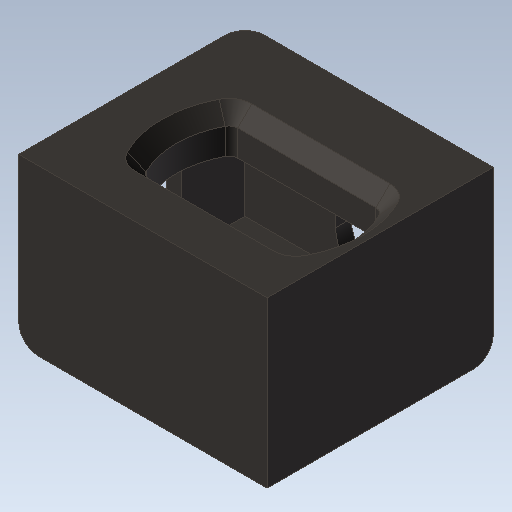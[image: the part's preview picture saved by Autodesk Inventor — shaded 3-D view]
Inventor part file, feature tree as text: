
AUTODESK INVENTOR PART (.ipt)
format: ipt  version: 2020 (Build 240168000, 168)  size: 167,424 bytes
history: mixed  units: mm
features: fillet x1, imported_body x1
ambient origin geometry x8: Origin, YZ Plane, XZ Plane, XY Plane, X Axis, Y Axis, Z Axis, Center Point
bodies: Solid1 (imported_parasolid)
feature tree (2):
  fillet  "Fillet2"  [1 undecoded]
  imported_body  NMx_Import_Brep_tag  [imported B-rep: ~18 faces, bbox_mm=[164.338, 79.502, 149.352]]
note: 1 required parameter value undecoded (feature->parameter linkage not recoverable at this tier; creation-order binding heuristic only, values carry confidence <= 0.55)
